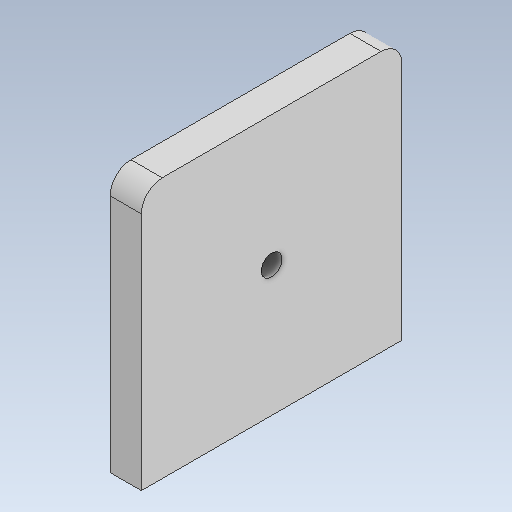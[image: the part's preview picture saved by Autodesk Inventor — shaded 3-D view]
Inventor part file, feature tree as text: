
AUTODESK INVENTOR PART (.ipt)
format: ipt  version: 2021 (Build 250183000, 183)  size: 114,176 bytes
history: native  units: mm
features: sketch x2, extrude x1, hole x1, fillet x1
ambient origin geometry x8: Origin, YZ Plane, XZ Plane, XY Plane, X Axis, Y Axis, Z Axis, Center Point
bodies: Solid1 (feature_tree)
feature tree (5):
  extrude  "Extrusion1"  Depth=50.0mm
  hole  "Hole1"  [1 undecoded]
  fillet  "Fillet1"  Radius=6.0mm
  sketch  "Sketch1"  dims[d0=50.0mm d1=50.0mm]
  sketch  "Sketch2"  dims[d2=25.0mm d3=25.0mm d4=6.0mm d5=0.0mm d6=4.0mm d7=6.0mm d8=4.0mm d9=2.0mm d10=90.0deg d11=8.0mm d12=20.594885mm d13=4.0mm]
note: 1 required parameter value undecoded (feature->parameter linkage not recoverable at this tier; creation-order binding heuristic only, values carry confidence <= 0.55)
